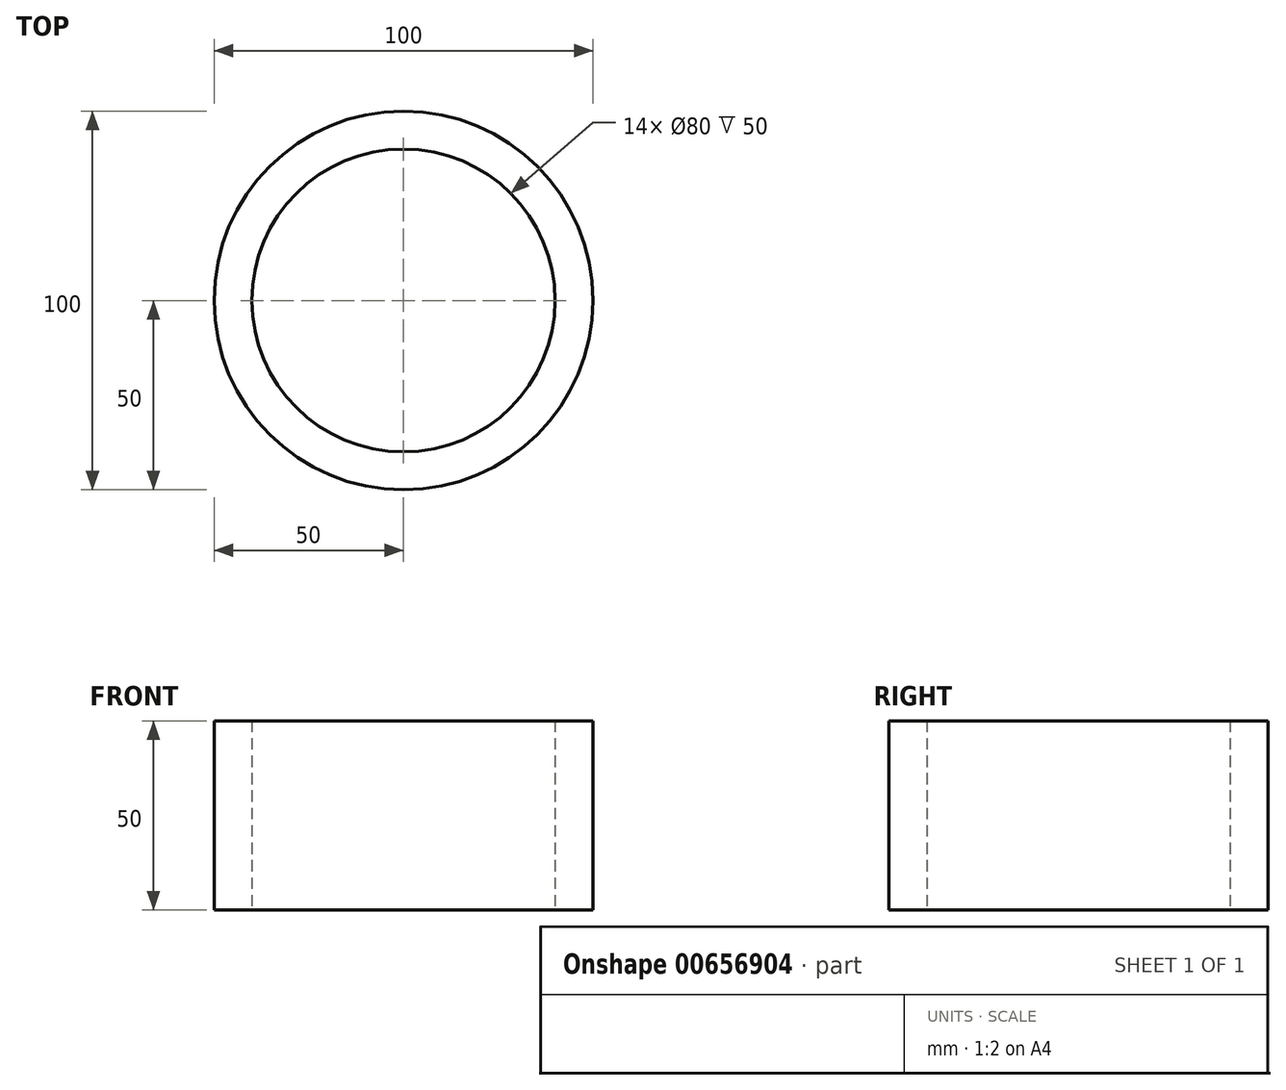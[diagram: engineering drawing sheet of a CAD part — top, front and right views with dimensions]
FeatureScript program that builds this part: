
annotation { "Feature Type Name" : "Feature", "Feature Type Description" : "" }
export const myFeature = defineFeature(function(context is Context, id is Id, definition is map)
    precondition{}
    {
        {
            var Q0;
            Q0=qCreatedBy(makeId("Top.planeOp"),FACE);
            var sketch = newSketch(context, id + "F0", { "sketchPlane" : qUnion([Q0])});
            skCircle(sketch, "E0", {"center": v(0, 0) * mm, "radius": 50 * mm});
            skCircle(sketch, "E1", {"center": v(0, 0) * mm, "radius": 40 * mm});
            skSolve(sketch);
        }
        {
            var Q0;
            Q0 = qSketchRegion(id + "F0", true);
            extrude(context, id + "F1", {"entities" : qUnion([Q0]), "depth" : 50 * mm, "offsetDistance" : 25 * mm});
        }
    });
